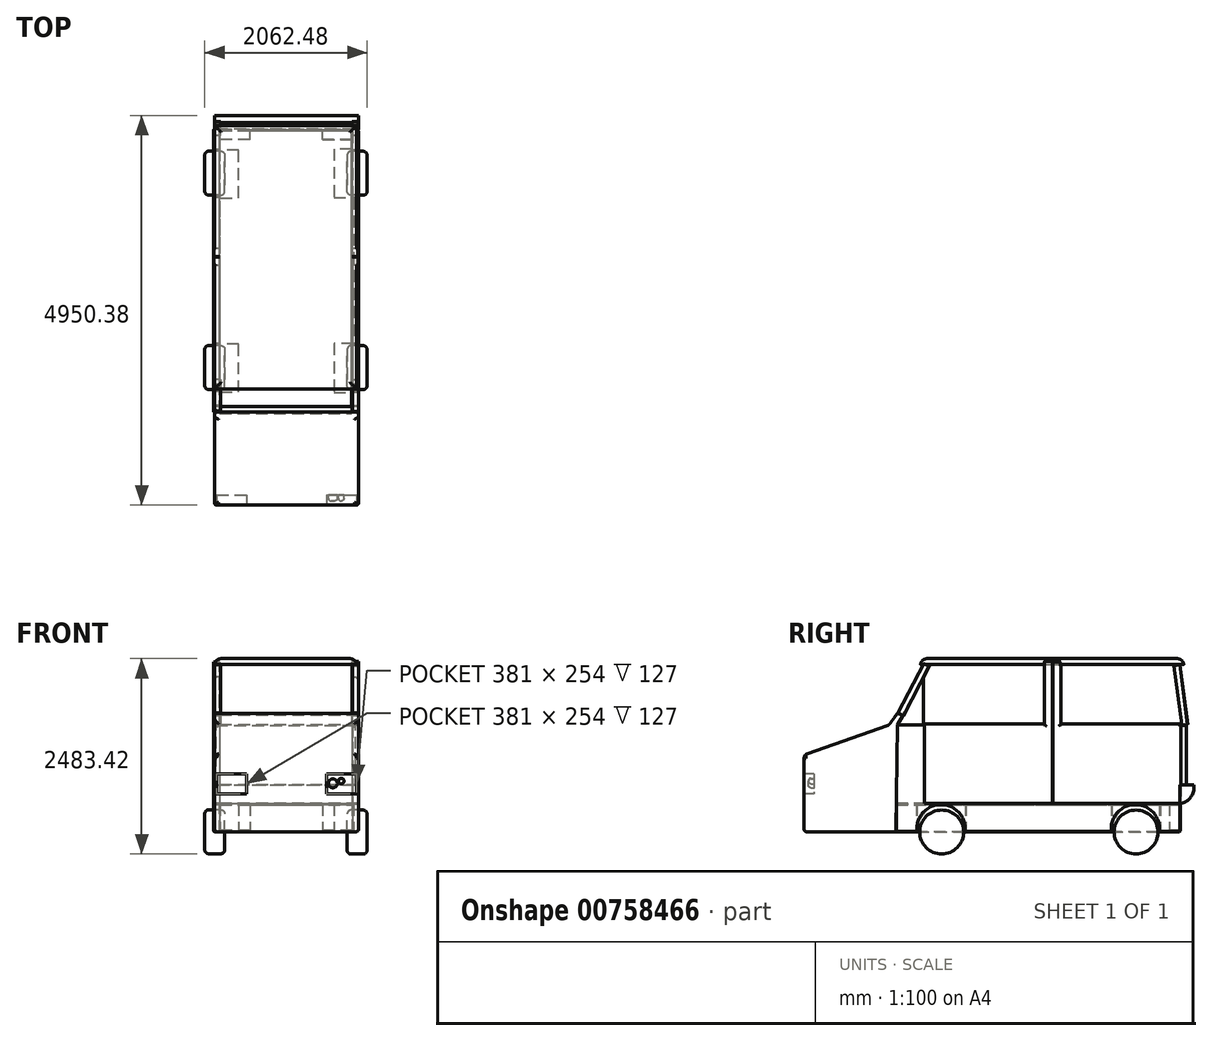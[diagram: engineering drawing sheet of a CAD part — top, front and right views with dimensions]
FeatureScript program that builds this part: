
annotation { "Feature Type Name" : "Feature", "Feature Type Description" : "" }
export const myFeature = defineFeature(function(context is Context, id is Id, definition is map)
    precondition{}
    {
        {
            var Q0;
            Q0=qCreatedBy(makeId("Top.planeOp"),FACE);
            var sketch = newSketch(context, id + "F0", { "sketchPlane" : qUnion([Q0])});
            skLineSegment(sketch, "E0.bottom", {"start": v(-913.42, 1731.15) * mm, "end": v(889.04, 1731.15) * mm});
            skLineSegment(sketch, "E0.top", {"start": v(-913.42, -1614.3) * mm, "end": v(889.04, -1614.3) * mm});
            skLineSegment(sketch, "E0.left", {"start": v(-913.42, 1731.15) * mm, "end": v(-913.42, -1614.3) * mm});
            skLineSegment(sketch, "E0.right", {"start": v(889.04, 1731.15) * mm, "end": v(889.04, -1614.3) * mm});
            skSolve(sketch);
        }
        {
            var Q0;
            Q0=makeQuery(id+"F0.imprint","IMPRINT",FACE,{"disambiguationData":[TD([[makeQuery(id+"F0.imprint","IMPRINT",EDGE,{"derivedFrom":sQuery(id+"F0.wireOp",EDGE,"E0.bottom")}),-1.0]])]});
            extrude(context, id + "F1", {"entities" : qUnion([Q0]), "surfaceOperationType" : NewSurfaceOperationType.ADD, "depth" : 76.2 * mm, "offsetDistance" : 25.4 * mm});
        }
        {
            var Q0;
            Q0=makeQuery(id+"F1.opExtrude","CAP_FACE",FACE,{"disambiguationData":[OSD([sQuery(id+"F0.wireOp",EDGE,"E0.bottom"),sQuery(id+"F0.wireOp",EDGE,"E0.top"),sQuery(id+"F0.wireOp",EDGE,"E0.left"),sQuery(id+"F0.wireOp",EDGE,"E0.right")])],"isStart":false});
            fillet(context, id + "F2", {"entities" : qUnion([Q0]), "radius" : 85.85 * mm, "tangentPropagation" : true, "allowEdgeOverflow" : false});
        }
        {
            var Q0;
            Q0=qCreatedBy(makeId("Right.planeOp"),FACE);
            var sketch = newSketch(context, id + "F3", { "sketchPlane" : qUnion([Q0])});
            skLineSegment(sketch, "E1.bottom", {"start": v(-1620.77, -101.5) * mm, "end": v(-1948.72, -732.58) * mm});
            skLineSegment(sketch, "E1.top", {"start": v(-1553.16, -136.64) * mm, "end": v(-1881.1, -767.72) * mm});
            skLineSegment(sketch, "E1.left", {"start": v(-1620.77, -101.5) * mm, "end": v(-1553.16, -136.64) * mm});
            skLineSegment(sketch, "E1.right", {"start": v(-1948.72, -732.58) * mm, "end": v(-1881.1, -767.72) * mm});
            skSolve(sketch);
        }
        {
            var Q0;
            Q0=makeQuery(id+"F3.imprint","IMPRINT",FACE,{"disambiguationData":[TD([[makeQuery(id+"F3.imprint","IMPRINT",EDGE,{"derivedFrom":sQuery(id+"F3.wireOp",EDGE,"E1.bottom")}),1.0]])]});
            extrude(context, id + "F4", {"entities" : qUnion([Q0]), "operationType" : NewBodyOperationType.ADD, "depth" : 76.2 * mm, "offsetDistance" : 25.4 * mm});
        }
        {
            var Q0;
            Q0=makeQuery(id+"F4.opExtrude","SWEPT_BODY",BODY,{"disambiguationData":[OSD([sQuery(id+"F3.wireOp",EDGE,"E1.bottom"),sQuery(id+"F3.wireOp",EDGE,"E1.top"),sQuery(id+"F3.wireOp",EDGE,"E1.left"),sQuery(id+"F3.wireOp",EDGE,"E1.right")])]});
            transform(context, id + "F5", {"entities" : qUnion([Q0]), "transformType" : TransformType.TRANSLATION_3D, "dx" : -914.4 * mm, "dy" : 0 * mm, "dz" : 116.84 * mm, "makeCopy" : false});
        }
        {
            var Q0;
            Q0=qCreatedBy(makeId("Right.planeOp"),FACE);
            var sketch = newSketch(context, id + "F6", { "sketchPlane" : qUnion([Q0])});
            skLineSegment(sketch, "E2.bottom", {"start": v(-1624.83, -94.97) * mm, "end": v(-1952.78, -726.04) * mm});
            skLineSegment(sketch, "E2.top", {"start": v(-1557.21, -130.1) * mm, "end": v(-1885.16, -761.18) * mm});
            skLineSegment(sketch, "E2.left", {"start": v(-1624.83, -94.97) * mm, "end": v(-1557.21, -130.1) * mm});
            skLineSegment(sketch, "E2.right", {"start": v(-1952.78, -726.04) * mm, "end": v(-1885.16, -761.18) * mm});
            skSolve(sketch);
        }
        {
            var Q0;
            Q0 = qSketchRegion(id + "F6", true);
            extrude(context, id + "F7", {"entities" : qUnion([Q0]), "depth" : 76.2 * mm, "offsetDistance" : 25.4 * mm});
        }
        {
            var Q0;
            Q0=makeQuery(id+"F7.opExtrude","SWEPT_BODY",BODY,{"disambiguationData":[OSD([sQuery(id+"F6.wireOp",EDGE,"E2.bottom"),sQuery(id+"F6.wireOp",EDGE,"E2.top"),sQuery(id+"F6.wireOp",EDGE,"E2.left"),sQuery(id+"F6.wireOp",EDGE,"E2.right")])]});
            transform(context, id + "F8", {"entities" : qUnion([Q0]), "transformType" : TransformType.TRANSLATION_3D, "dx" : 835.66 * mm, "dy" : -2.54 * mm, "dz" : 109.22 * mm, "makeCopy" : false});
        }
        {
            var Q0;
            Q0=qCreatedBy(makeId("Right.planeOp"),FACE);
            var sketch = newSketch(context, id + "F9", { "sketchPlane" : qUnion([Q0])});
            skLineSegment(sketch, "E3.bottom", {"start": v(1547.92, -14.01) * mm, "end": v(1647.91, -769.42) * mm});
            skLineSegment(sketch, "E3.top", {"start": v(1623.46, -4.01) * mm, "end": v(1723.46, -759.42) * mm});
            skLineSegment(sketch, "E3.left", {"start": v(1547.92, -14.01) * mm, "end": v(1623.46, -4.01) * mm});
            skLineSegment(sketch, "E3.right", {"start": v(1647.91, -769.42) * mm, "end": v(1723.46, -759.42) * mm});
            skSolve(sketch);
        }
        {
            var Q0;
            Q0 = qSketchRegion(id + "F9", true);
            extrude(context, id + "F10", {"entities" : qUnion([Q0]), "depth" : 76.2 * mm, "offsetDistance" : 25.4 * mm});
        }
        {
            var Q0;
            Q0=makeQuery(id+"F10.opExtrude","SWEPT_BODY",BODY,{"disambiguationData":[OSD([sQuery(id+"F9.wireOp",EDGE,"E3.bottom"),sQuery(id+"F9.wireOp",EDGE,"E3.top"),sQuery(id+"F9.wireOp",EDGE,"E3.left"),sQuery(id+"F9.wireOp",EDGE,"E3.right")])]});
            transform(context, id + "F11", {"entities" : qUnion([Q0]), "transformType" : TransformType.TRANSLATION_3D, "dx" : 828.04 * mm, "dy" : 0 * mm, "dz" : 0 * mm, "makeCopy" : false});
        }
        {
            var Q0;
            Q0=qCreatedBy(makeId("Right.planeOp"),FACE);
            var sketch = newSketch(context, id + "F12", { "sketchPlane" : qUnion([Q0])});
            skLineSegment(sketch, "E4.bottom", {"start": v(1549.53, -22.95) * mm, "end": v(1649.53, -778.36) * mm});
            skLineSegment(sketch, "E4.top", {"start": v(1625.08, -12.95) * mm, "end": v(1725.07, -768.36) * mm});
            skLineSegment(sketch, "E4.left", {"start": v(1549.53, -22.95) * mm, "end": v(1625.08, -12.95) * mm});
            skLineSegment(sketch, "E4.right", {"start": v(1649.53, -778.36) * mm, "end": v(1725.07, -768.36) * mm});
            skSolve(sketch);
        }
        {
            var Q0;
            Q0 = qSketchRegion(id + "F12", true);
            extrude(context, id + "F13", {"entities" : qUnion([Q0]), "depth" : 76.2 * mm, "offsetDistance" : 25.4 * mm});
        }
        {
            var Q0;
            Q0=makeQuery(id+"F13.opExtrude","SWEPT_BODY",BODY,{"disambiguationData":[OSD([sQuery(id+"F12.wireOp",EDGE,"E4.bottom"),sQuery(id+"F12.wireOp",EDGE,"E4.top"),sQuery(id+"F12.wireOp",EDGE,"E4.left"),sQuery(id+"F12.wireOp",EDGE,"E4.right")])]});
            transform(context, id + "F14", {"entities" : qUnion([Q0]), "transformType" : TransformType.TRANSLATION_3D, "dx" : -919.48 * mm, "dy" : 0 * mm, "dz" : 10.16 * mm, "makeCopy" : false});
        }
        {
            var Q0;
            Q0=qCreatedBy(makeId("Front.planeOp"),FACE);
            var sketch = newSketch(context, id + "F15", { "sketchPlane" : qUnion([Q0])});
            skLineSegment(sketch, "E5.bottom", {"start": v(910.85, -1501.62) * mm, "end": v(-917.95, -1501.62) * mm});
            skLineSegment(sketch, "E5.top", {"start": v(910.85, -1739) * mm, "end": v(-917.95, -1739) * mm});
            skLineSegment(sketch, "E5.left", {"start": v(910.85, -1501.62) * mm, "end": v(910.85, -1739) * mm});
            skLineSegment(sketch, "E5.right", {"start": v(-917.95, -1501.62) * mm, "end": v(-917.95, -1739) * mm});
            skSolve(sketch);
        }
        {
            var Q0;
            Q0 = qSketchRegion(id + "F15", true);
            extrude(context, id + "F16", {"entities" : qUnion([Q0]), "depth" : 177.8 * mm, "offsetDistance" : 25.4 * mm});
        }
        {
            var Q0;
            Q0=makeQuery(id+"F16.opExtrude","SWEPT_BODY",BODY,{"disambiguationData":[OSD([sQuery(id+"F15.wireOp",EDGE,"E5.bottom"),sQuery(id+"F15.wireOp",EDGE,"E5.top"),sQuery(id+"F15.wireOp",EDGE,"E5.left"),sQuery(id+"F15.wireOp",EDGE,"E5.right")])]});
            transform(context, id + "F17", {"entities" : qUnion([Q0]), "transformType" : TransformType.TRANSLATION_3D, "dx" : 0 * mm, "dy" : 1803.4 * mm, "dz" : -25.4 * mm, "makeCopy" : false});
        }
        {
            var Q0;
            Q0=makeQuery(id+"F16.opExtrude","CAP_EDGE",EDGE,{"disambiguationData":[OSD([sQuery(id+"F15.wireOp",EDGE,"E5.top")])],"isStart":true});
            fillet(context, id + "F18", {"entities" : qUnion([Q0]), "radius" : 202.36 * mm, "tangentPropagation" : true, "allowEdgeOverflow" : false});
        }
        {
            var Q0;
            Q0=qCreatedBy(makeId("Right.planeOp"),FACE);
            var sketch = newSketch(context, id + "F19", { "sketchPlane" : qUnion([Q0])});
            skLineSegment(sketch, "E6.bottom", {"start": v(1625.6, -744.32) * mm, "end": v(0, -744.32) * mm});
            skLineSegment(sketch, "E6.top", {"start": v(1625.6, -1751.35) * mm, "end": v(0, -1751.35) * mm});
            skLineSegment(sketch, "E6.left", {"start": v(1625.6, -744.32) * mm, "end": v(1625.6, -1751.35) * mm});
            skLineSegment(sketch, "E6.right", {"start": v(0, -744.32) * mm, "end": v(0, -1751.35) * mm});
            skLineSegment(sketch, "E7.top", {"start": v(0, 47.93) * mm, "end": v(101.6, 47.93) * mm});
            skLineSegment(sketch, "E7.left", {"start": v(0, -744.32) * mm, "end": v(0, 47.93) * mm});
            skLineSegment(sketch, "E7.right", {"start": v(101.6, -744.32) * mm, "end": v(101.6, 47.93) * mm});
            skSolve(sketch);
        }
        {
            var Q0;
            Q0 = qSketchRegion(id + "F19", true);
            extrude(context, id + "F20", {"entities" : qUnion([Q0]), "depth" : 76.2 * mm, "offsetDistance" : 25.4 * mm});
        }
        {
            var Q0;
            Q0=makeQuery(id+"F20.opExtrude","SWEPT_BODY",BODY,{"disambiguationData":[OSD([sQuery(id+"F19.wireOp",EDGE,"E6.bottom"),sQuery(id+"F19.wireOp",EDGE,"E6.top"),sQuery(id+"F19.wireOp",EDGE,"E6.left"),sQuery(id+"F19.wireOp",EDGE,"E6.right"),sQuery(id+"F19.wireOp",EDGE,"E7.top"),sQuery(id+"F19.wireOp",EDGE,"E7.left"),sQuery(id+"F19.wireOp",EDGE,"E7.right")])]});
            transform(context, id + "F21", {"entities" : qUnion([Q0]), "transformType" : TransformType.TRANSLATION_3D, "dx" : -929.64 * mm, "dy" : 10.16 * mm, "dz" : -12.7 * mm, "makeCopy" : false});
        }
        {
            var Q0;
            Q0=qCreatedBy(makeId("Right.planeOp"),FACE);
            var sketch = newSketch(context, id + "F22", { "sketchPlane" : qUnion([Q0])});
            skLineSegment(sketch, "E8.bottom", {"start": v(1625.6, -743.62) * mm, "end": v(0, -743.62) * mm});
            skLineSegment(sketch, "E8.top", {"start": v(1625.6, -1750.65) * mm, "end": v(0, -1750.65) * mm});
            skLineSegment(sketch, "E8.left", {"start": v(1625.6, -743.62) * mm, "end": v(1625.6, -1750.65) * mm});
            skLineSegment(sketch, "E8.right", {"start": v(0, -743.62) * mm, "end": v(0, -1750.65) * mm});
            skLineSegment(sketch, "E9.top", {"start": v(0, 48.63) * mm, "end": v(101.6, 48.63) * mm});
            skLineSegment(sketch, "E9.left", {"start": v(0, -743.62) * mm, "end": v(0, 48.63) * mm});
            skLineSegment(sketch, "E9.right", {"start": v(101.6, -743.62) * mm, "end": v(101.6, 48.63) * mm});
            skSolve(sketch);
        }
        {
            var Q0;
            Q0 = qSketchRegion(id + "F22", true);
            extrude(context, id + "F23", {"entities" : qUnion([Q0]), "depth" : 76.2 * mm, "offsetDistance" : 25.4 * mm});
        }
        {
            var Q0;
            Q0=makeQuery(id+"F23.opExtrude","SWEPT_BODY",BODY,{"disambiguationData":[OSD([sQuery(id+"F22.wireOp",EDGE,"E8.bottom"),sQuery(id+"F22.wireOp",EDGE,"E8.top"),sQuery(id+"F22.wireOp",EDGE,"E8.left"),sQuery(id+"F22.wireOp",EDGE,"E8.right"),sQuery(id+"F22.wireOp",EDGE,"E9.top"),sQuery(id+"F22.wireOp",EDGE,"E9.left"),sQuery(id+"F22.wireOp",EDGE,"E9.right")])]});
            transform(context, id + "F24", {"entities" : qUnion([Q0]), "transformType" : TransformType.TRANSLATION_3D, "dx" : 830.58 * mm, "dy" : 10.16 * mm, "dz" : -12.7 * mm, "makeCopy" : false});
        }
        {
            var Q0;
            Q0=qCreatedBy(makeId("Right.planeOp"),FACE);
            var sketch = newSketch(context, id + "F25", { "sketchPlane" : qUnion([Q0])});
            skLineSegment(sketch, "E10.bottom", {"start": v(9.66, -772.73) * mm, "end": v(-1615.94, -772.73) * mm});
            skLineSegment(sketch, "E10.top", {"start": v(9.66, -1779.59) * mm, "end": v(-1615.94, -1779.59) * mm});
            skLineSegment(sketch, "E10.left", {"start": v(9.66, -772.73) * mm, "end": v(9.66, -1779.59) * mm});
            skLineSegment(sketch, "E10.right", {"start": v(-1615.94, -772.73) * mm, "end": v(-1615.94, -1779.59) * mm});
            skLineSegment(sketch, "E11.top", {"start": v(-94.48, 19.52) * mm, "end": v(7.12, 19.52) * mm});
            skLineSegment(sketch, "E11.left", {"start": v(-94.48, -772.73) * mm, "end": v(-94.48, 19.52) * mm});
            skLineSegment(sketch, "E11.right", {"start": v(7.12, -772.73) * mm, "end": v(7.12, 19.52) * mm});
            skSolve(sketch);
        }
        {
            var Q0;
            Q0=makeQuery(id+"F25.imprint","IMPRINT",FACE,{"disambiguationData":[TD([[makeQuery(id+"F25.imprint","IMPRINT",EDGE,{"derivedFrom":sQuery(id+"F25.wireOp",EDGE,"E10.top")}),-1.0]])]});
            var Q1;
            Q1=makeQuery(id+"F25.imprint","IMPRINT",FACE,{"disambiguationData":[TD([[makeQuery(id+"F25.imprint","IMPRINT",EDGE,{"derivedFrom":sQuery(id+"F25.wireOp",EDGE,"E11.top")}),-1.0]])]});
            extrude(context, id + "F26", {"entities" : qUnion([Q0, Q1]), "oppositeDirection" : true, "depth" : 76.2 * mm, "offsetDistance" : 25.4 * mm});
        }
        {
            var Q0;
            Q0=makeQuery(id+"F26.opExtrude","SWEPT_BODY",BODY,{"disambiguationData":[OSD([sQuery(id+"F25.wireOp",EDGE,"E10.bottom"),sQuery(id+"F25.wireOp",EDGE,"E10.top"),sQuery(id+"F25.wireOp",EDGE,"E10.left"),sQuery(id+"F25.wireOp",EDGE,"E10.right"),sQuery(id+"F25.wireOp",EDGE,"E11.top"),sQuery(id+"F25.wireOp",EDGE,"E11.left"),sQuery(id+"F25.wireOp",EDGE,"E11.right")])]});
            transform(context, id + "F27", {"entities" : qUnion([Q0]), "transformType" : TransformType.TRANSLATION_3D, "dx" : -850.9 * mm, "dy" : 0 * mm, "dz" : 15.24 * mm, "makeCopy" : false});
        }
        {
            var Q0;
            Q0=qCreatedBy(makeId("Right.planeOp"),FACE);
            var sketch = newSketch(context, id + "F28", { "sketchPlane" : qUnion([Q0])});
            skLineSegment(sketch, "E12.bottom", {"start": v(-4.33, -770.44) * mm, "end": v(-1629.93, -770.44) * mm});
            skLineSegment(sketch, "E12.top", {"start": v(-4.33, -1777.3) * mm, "end": v(-1629.93, -1777.3) * mm});
            skLineSegment(sketch, "E12.left", {"start": v(-4.33, -770.44) * mm, "end": v(-4.33, -1777.3) * mm});
            skLineSegment(sketch, "E12.right", {"start": v(-1629.93, -770.44) * mm, "end": v(-1629.93, -1777.3) * mm});
            skLineSegment(sketch, "E13.top", {"start": v(-108.47, 21.82) * mm, "end": v(-6.87, 21.82) * mm});
            skLineSegment(sketch, "E13.left", {"start": v(-108.47, -770.44) * mm, "end": v(-108.47, 21.82) * mm});
            skLineSegment(sketch, "E13.right", {"start": v(-6.87, -770.44) * mm, "end": v(-6.87, 21.82) * mm});
            skSolve(sketch);
        }
        {
            var Q0;
            Q0 = qSketchRegion(id + "F28", true);
            extrude(context, id + "F29", {"entities" : qUnion([Q0]), "depth" : 76.2 * mm, "offsetDistance" : 25.4 * mm});
        }
        {
            var Q0;
            Q0=makeQuery(id+"F29.opExtrude","SWEPT_BODY",BODY,{"disambiguationData":[OSD([sQuery(id+"F28.wireOp",EDGE,"E12.bottom"),sQuery(id+"F28.wireOp",EDGE,"E12.top"),sQuery(id+"F28.wireOp",EDGE,"E12.left"),sQuery(id+"F28.wireOp",EDGE,"E12.right"),sQuery(id+"F28.wireOp",EDGE,"E13.top"),sQuery(id+"F28.wireOp",EDGE,"E13.left"),sQuery(id+"F28.wireOp",EDGE,"E13.right")])]});
            transform(context, id + "F30", {"entities" : qUnion([Q0]), "transformType" : TransformType.TRANSLATION_3D, "dx" : 838.2 * mm, "dy" : 12.7 * mm, "dz" : 15.24 * mm, "makeCopy" : false});
        }
        {
            var Q0;
            Q0=qCreatedBy(makeId("Right.planeOp"),FACE);
            var sketch = newSketch(context, id + "F31", { "sketchPlane" : qUnion([Q0])});
            skLineSegment(sketch, "E14", {"start": v(-1629.73, -766.93) * mm, "end": v(-1967.97, -766.93) * mm});
            skLineSegment(sketch, "E15", {"start": v(-1629.73, -766.93) * mm, "end": v(-1629.73, -162.86) * mm});
            skLineSegment(sketch, "E16", {"start": v(-1629.73, -162.86) * mm, "end": v(-1967.97, -766.93) * mm});
            skSolve(sketch);
        }
        {
            var Q0;
            Q0 = qSketchRegion(id + "F31", true);
            extrude(context, id + "F32", {"entities" : qUnion([Q0]), "depth" : 76.2 * mm, "offsetDistance" : 25.4 * mm});
        }
        {
            var Q0;
            Q0=makeQuery(id+"F32.opExtrude","SWEPT_BODY",BODY,{"disambiguationData":[OSD([sQuery(id+"F31.wireOp",EDGE,"E14"),sQuery(id+"F31.wireOp",EDGE,"E15"),sQuery(id+"F31.wireOp",EDGE,"E16")])]});
            transform(context, id + "F33", {"entities" : qUnion([Q0]), "transformType" : TransformType.TRANSLATION_3D, "dx" : 828.04 * mm, "dy" : 0 * mm, "dz" : 0 * mm, "makeCopy" : false});
        }
        {
            var Q0;
            Q0=qCreatedBy(makeId("Right.planeOp"),FACE);
            var sketch = newSketch(context, id + "F34", { "sketchPlane" : qUnion([Q0])});
            skLineSegment(sketch, "E17", {"start": v(-1630.86, -760.73) * mm, "end": v(-1969.1, -760.73) * mm});
            skLineSegment(sketch, "E18", {"start": v(-1630.86, -760.73) * mm, "end": v(-1630.86, -156.66) * mm});
            skLineSegment(sketch, "E19", {"start": v(-1630.86, -156.66) * mm, "end": v(-1969.1, -760.73) * mm});
            skSolve(sketch);
        }
        {
            var Q0;
            Q0 = qSketchRegion(id + "F34", true);
            extrude(context, id + "F35", {"entities" : qUnion([Q0]), "depth" : 76.2 * mm, "offsetDistance" : 25.4 * mm});
        }
        {
            var Q0;
            Q0=makeQuery(id+"F35.opExtrude","SWEPT_BODY",BODY,{"disambiguationData":[OSD([sQuery(id+"F34.wireOp",EDGE,"E17"),sQuery(id+"F34.wireOp",EDGE,"E18"),sQuery(id+"F34.wireOp",EDGE,"E19")])]});
            transform(context, id + "F36", {"entities" : qUnion([Q0]), "transformType" : TransformType.TRANSLATION_3D, "dx" : -914.4 * mm, "dy" : 0 * mm, "dz" : 0 * mm, "makeCopy" : false});
        }
        {
            var Q0;
            Q0=qCreatedBy(makeId("Right.planeOp"),FACE);
            var sketch = newSketch(context, id + "F37", { "sketchPlane" : qUnion([Q0])});
            skLineSegment(sketch, "E20", {"start": v(1624.35, -1763.38) * mm, "end": v(1624.35, -2119.01) * mm});
            skLineSegment(sketch, "E21", {"start": v(1624.35, -2119.01) * mm, "end": v(1361.69, -2119.01) * mm});
            skArc(sketch, "E22", {"start": v(1361.69, -2119.01) * mm, "mid": v(1059.19, -1776.84) * mm, "end": v(756.69, -2119.01) * mm});
            skLineSegment(sketch, "E23", {"start": v(-1975.22, -764.67) * mm, "end": v(-1975.22, -2119.01) * mm});
            skLineSegment(sketch, "E24", {"start": v(-1975.22, -2119.01) * mm, "end": v(-1711.82, -2119.01) * mm});
            skArc(sketch, "E25", {"start": v(-1106.82, -2119.01) * mm, "mid": v(-1409.32, -1776.84) * mm, "end": v(-1711.82, -2119.01) * mm});
            skLineSegment(sketch, "E26", {"start": v(-1106.82, -2119.01) * mm, "end": v(756.69, -2119.01) * mm});
            skLineSegment(sketch, "E27", {"start": v(-1975.22, -764.67) * mm, "end": v(-1620.55, -764.67) * mm});
            skLineSegment(sketch, "E28", {"start": v(-1620.55, -764.67) * mm, "end": v(-1620.55, -1765.04) * mm});
            skLineSegment(sketch, "E29", {"start": v(-1620.55, -1765.04) * mm, "end": v(1624.35, -1763.38) * mm});
            skSolve(sketch);
        }
        {
            var Q0;
            Q0 = qSketchRegion(id + "F37", true);
            extrude(context, id + "F38", {"entities" : qUnion([Q0]), "depth" : 76.2 * mm, "offsetDistance" : 25.4 * mm});
        }
        {
            var Q0;
            Q0=makeQuery(id+"F38.opExtrude","SWEPT_BODY",BODY,{"disambiguationData":[OSD([sQuery(id+"F37.wireOp",EDGE,"E20"),sQuery(id+"F37.wireOp",EDGE,"E21"),sQuery(id+"F37.wireOp",EDGE,"E22"),sQuery(id+"F37.wireOp",EDGE,"E23"),sQuery(id+"F37.wireOp",EDGE,"E24"),sQuery(id+"F37.wireOp",EDGE,"E25"),sQuery(id+"F37.wireOp",EDGE,"E26"),sQuery(id+"F37.wireOp",EDGE,"E27"),sQuery(id+"F37.wireOp",EDGE,"E28"),sQuery(id+"F37.wireOp",EDGE,"E29")])]});
            transform(context, id + "F39", {"entities" : qUnion([Q0]), "transformType" : TransformType.TRANSLATION_3D, "dx" : 833.12 * mm, "dy" : 0 * mm, "dz" : 0 * mm, "makeCopy" : false});
        }
        {
            var Q0;
            Q0=qCreatedBy(makeId("Right.planeOp"),FACE);
            var sketch = newSketch(context, id + "F40", { "sketchPlane" : qUnion([Q0])});
            skLineSegment(sketch, "E30", {"start": v(1632.28, -1771.88) * mm, "end": v(1632.28, -2127.5) * mm});
            skLineSegment(sketch, "E31", {"start": v(1632.28, -2127.5) * mm, "end": v(1369.62, -2127.5) * mm});
            skArc(sketch, "E32", {"start": v(1369.62, -2127.5) * mm, "mid": v(1067.12, -1785.34) * mm, "end": v(764.61, -2127.5) * mm});
            skLineSegment(sketch, "E33", {"start": v(-1967.3, -773.17) * mm, "end": v(-1967.3, -2127.5) * mm});
            skLineSegment(sketch, "E34", {"start": v(-1967.3, -2127.5) * mm, "end": v(-1703.9, -2127.5) * mm});
            skArc(sketch, "E35", {"start": v(-1098.9, -2127.5) * mm, "mid": v(-1401.4, -1785.34) * mm, "end": v(-1703.9, -2127.5) * mm});
            skLineSegment(sketch, "E36", {"start": v(-1098.9, -2127.5) * mm, "end": v(764.61, -2127.5) * mm});
            skLineSegment(sketch, "E37", {"start": v(-1967.3, -773.17) * mm, "end": v(-1612.62, -773.17) * mm});
            skLineSegment(sketch, "E38", {"start": v(-1612.62, -773.17) * mm, "end": v(-1612.62, -1773.54) * mm});
            skLineSegment(sketch, "E39", {"start": v(-1612.62, -1773.54) * mm, "end": v(1632.28, -1771.88) * mm});
            skSolve(sketch);
        }
        {
            var Q0;
            Q0 = qSketchRegion(id + "F40", true);
            extrude(context, id + "F41", {"entities" : qUnion([Q0]), "depth" : 76.2 * mm, "offsetDistance" : 25.4 * mm});
        }
        {
            var Q0;
            Q0=makeQuery(id+"F41.opExtrude","SWEPT_BODY",BODY,{"disambiguationData":[OSD([sQuery(id+"F40.wireOp",EDGE,"E30"),sQuery(id+"F40.wireOp",EDGE,"E31"),sQuery(id+"F40.wireOp",EDGE,"E32"),sQuery(id+"F40.wireOp",EDGE,"E33"),sQuery(id+"F40.wireOp",EDGE,"E34"),sQuery(id+"F40.wireOp",EDGE,"E35"),sQuery(id+"F40.wireOp",EDGE,"E36"),sQuery(id+"F40.wireOp",EDGE,"E37"),sQuery(id+"F40.wireOp",EDGE,"E38"),sQuery(id+"F40.wireOp",EDGE,"E39")])]});
            transform(context, id + "F42", {"entities" : qUnion([Q0]), "transformType" : TransformType.TRANSLATION_3D, "dx" : -929.64 * mm, "dy" : 0 * mm, "dz" : 0 * mm, "makeCopy" : false});
        }
        {
            var Q0;
            Q0=qCreatedBy(makeId("Top.planeOp"),FACE);
            var sketch = newSketch(context, id + "F43", { "sketchPlane" : qUnion([Q0])});
            skLineSegment(sketch, "E40", {"start": v(828.42, -1713.23) * mm, "end": v(828.42, -1973.46) * mm});
            skLineSegment(sketch, "E41", {"start": v(828.42, -1973.46) * mm, "end": v(-844.52, -1973.46) * mm});
            skLineSegment(sketch, "E42", {"start": v(-844.52, 1620.26) * mm, "end": v(828.42, 1620.26) * mm});
            skLineSegment(sketch, "E43", {"start": v(828.42, 1620.26) * mm, "end": v(828.42, 1378.6) * mm});
            skLineSegment(sketch, "E44", {"start": v(828.42, 1378.6) * mm, "end": v(599.16, 1378.6) * mm});
            skLineSegment(sketch, "E45", {"start": v(599.16, 1378.6) * mm, "end": v(599.16, 759) * mm});
            skLineSegment(sketch, "E46", {"start": v(599.16, 759) * mm, "end": v(847, 759) * mm});
            skLineSegment(sketch, "E47", {"start": v(847, 759) * mm, "end": v(847, -1093.62) * mm});
            skLineSegment(sketch, "E48", {"start": v(847, -1093.62) * mm, "end": v(599.16, -1093.62) * mm});
            skLineSegment(sketch, "E49", {"start": v(599.16, -1093.62) * mm, "end": v(599.16, -1719.42) * mm});
            skLineSegment(sketch, "E50", {"start": v(599.16, -1719.42) * mm, "end": v(828.42, -1713.23) * mm});
            skLineSegment(sketch, "E51", {"start": v(-844.52, -1973.46) * mm, "end": v(-844.52, -1713.23) * mm});
            skLineSegment(sketch, "E52", {"start": v(-844.52, -1713.23) * mm, "end": v(-609.07, -1713.23) * mm});
            skLineSegment(sketch, "E53", {"start": v(-609.07, -1713.23) * mm, "end": v(-609.07, -1099.82) * mm});
            skLineSegment(sketch, "E54", {"start": v(-609.07, -1099.82) * mm, "end": v(-844.52, -1099.82) * mm});
            skLineSegment(sketch, "E55", {"start": v(-844.52, -1099.82) * mm, "end": v(-844.52, 752.8) * mm});
            skLineSegment(sketch, "E56", {"start": v(-844.52, 752.8) * mm, "end": v(-609.07, 752.8) * mm});
            skLineSegment(sketch, "E57", {"start": v(-609.07, 752.8) * mm, "end": v(-609.07, 1366.22) * mm});
            skLineSegment(sketch, "E58", {"start": v(-609.07, 1366.22) * mm, "end": v(-844.52, 1366.22) * mm});
            skLineSegment(sketch, "E59", {"start": v(-844.52, 1366.22) * mm, "end": v(-844.52, 1620.26) * mm});
            skSolve(sketch);
        }
        {
            var Q0;
            Q0 = qSketchRegion(id + "F43", true);
            extrude(context, id + "F44", {"entities" : qUnion([Q0]), "depth" : 355.6 * mm, "offsetDistance" : 25.4 * mm});
        }
        {
            var Q0;
            Q0=makeQuery(id+"F44.opExtrude","SWEPT_BODY",BODY,{"disambiguationData":[OSD([sQuery(id+"F43.wireOp",EDGE,"E40"),sQuery(id+"F43.wireOp",EDGE,"E41"),sQuery(id+"F43.wireOp",EDGE,"E42"),sQuery(id+"F43.wireOp",EDGE,"E43"),sQuery(id+"F43.wireOp",EDGE,"E44"),sQuery(id+"F43.wireOp",EDGE,"E45"),sQuery(id+"F43.wireOp",EDGE,"E46"),sQuery(id+"F43.wireOp",EDGE,"E47"),sQuery(id+"F43.wireOp",EDGE,"E48"),sQuery(id+"F43.wireOp",EDGE,"E49"),sQuery(id+"F43.wireOp",EDGE,"E50"),sQuery(id+"F43.wireOp",EDGE,"E51"),sQuery(id+"F43.wireOp",EDGE,"E52"),sQuery(id+"F43.wireOp",EDGE,"E53"),sQuery(id+"F43.wireOp",EDGE,"E54"),sQuery(id+"F43.wireOp",EDGE,"E55"),sQuery(id+"F43.wireOp",EDGE,"E56"),sQuery(id+"F43.wireOp",EDGE,"E57"),sQuery(id+"F43.wireOp",EDGE,"E58"),sQuery(id+"F43.wireOp",EDGE,"E59")])]});
            transform(context, id + "F45", {"entities" : qUnion([Q0]), "transformType" : TransformType.TRANSLATION_3D, "dx" : 0 * mm, "dy" : 0 * mm, "dz" : -2125.98 * mm, "makeCopy" : false});
        }
        {
            var Q0;
            Q0=qCreatedBy(makeId("Top.planeOp"),FACE);
            var sketch = newSketch(context, id + "F46", { "sketchPlane" : qUnion([Q0])});
            skLineSegment(sketch, "E60.bottom", {"start": v(-851.82, -1980.55) * mm, "end": v(825.7, -1980.55) * mm});
            skLineSegment(sketch, "E60.top", {"start": v(-851.82, 1612.18) * mm, "end": v(825.7, 1612.18) * mm});
            skLineSegment(sketch, "E60.left", {"start": v(-851.82, -1980.55) * mm, "end": v(-851.82, 1612.18) * mm});
            skLineSegment(sketch, "E60.right", {"start": v(825.7, -1980.55) * mm, "end": v(825.7, 1612.18) * mm});
            skSolve(sketch);
        }
        {
            var Q0;
            Q0 = qSketchRegion(id + "F46", true);
            extrude(context, id + "F47", {"entities" : qUnion([Q0]), "depth" : 25.4 * mm, "offsetDistance" : 25.4 * mm});
        }
        {
            var Q0;
            Q0=makeQuery(id+"F47.opExtrude","SWEPT_BODY",BODY,{"disambiguationData":[OSD([sQuery(id+"F46.wireOp",EDGE,"E60.bottom"),sQuery(id+"F46.wireOp",EDGE,"E60.top"),sQuery(id+"F46.wireOp",EDGE,"E60.left"),sQuery(id+"F46.wireOp",EDGE,"E60.right")])]});
            transform(context, id + "F48", {"entities" : qUnion([Q0]), "transformType" : TransformType.TRANSLATION_3D, "dx" : 0 * mm, "dy" : 0 * mm, "dz" : -1780.54 * mm, "makeCopy" : false});
        }
        {
            var Q0;
            Q0=qCreatedBy(makeId("Right.planeOp"),FACE);
            var sketch = newSketch(context, id + "F49", { "sketchPlane" : qUnion([Q0])});
            skLineSegment(sketch, "E61", {"start": v(-1962, -617.43) * mm, "end": v(-2068.8, -765.92) * mm});
            skLineSegment(sketch, "E62", {"start": v(-2068.8, -765.92) * mm, "end": v(-3146.98, -1146.38) * mm});
            skLineSegment(sketch, "E63", {"start": v(-3146.98, -1146.38) * mm, "end": v(-3146.98, -2122.05) * mm});
            skLineSegment(sketch, "E64", {"start": v(-3146.98, -2122.05) * mm, "end": v(-1978.53, -2122.05) * mm});
            skLineSegment(sketch, "E65", {"start": v(-1978.53, -2122.05) * mm, "end": v(-1962, -765.92) * mm});
            skLineSegment(sketch, "E66", {"start": v(-1962, -765.92) * mm, "end": v(-1895.44, -643.06) * mm});
            skLineSegment(sketch, "E67", {"start": v(-1895.44, -643.06) * mm, "end": v(-1962, -617.43) * mm});
            skSolve(sketch);
        }
        {
            var Q0;
            Q0 = qSketchRegion(id + "F49", true);
            extrude(context, id + "F50", {"entities" : qUnion([Q0]), "depth" : 1828.8 * mm, "offsetDistance" : 25.4 * mm});
        }
        {
            var Q0;
            Q0=makeQuery(id+"F50.opExtrude","SWEPT_BODY",BODY,{"disambiguationData":[OSD([sQuery(id+"F49.wireOp",EDGE,"E61"),sQuery(id+"F49.wireOp",EDGE,"E62"),sQuery(id+"F49.wireOp",EDGE,"E63"),sQuery(id+"F49.wireOp",EDGE,"E64"),sQuery(id+"F49.wireOp",EDGE,"E65"),sQuery(id+"F49.wireOp",EDGE,"E66"),sQuery(id+"F49.wireOp",EDGE,"E67")])]});
            transform(context, id + "F51", {"entities" : qUnion([Q0]), "transformType" : TransformType.TRANSLATION_3D, "dx" : -916.94 * mm, "dy" : 0 * mm, "dz" : 0 * mm, "makeCopy" : false});
        }
        {
            var Q0;
            Q0=qCreatedBy(makeId("Right.planeOp"),FACE);
            var sketch = newSketch(context, id + "F52", { "sketchPlane" : qUnion([Q0])});
            skCircle(sketch, "E68", {"center": v(1070, -2123.2) * mm, "radius": 279.4 * mm});
            skCircle(sketch, "E69", {"center": v(-1399.13, -2123.2) * mm, "radius": 279.4 * mm});
            skSolve(sketch);
        }
        {
            var Q0;
            Q0 = qSketchRegion(id + "F52", true);
            extrude(context, id + "F53", {"entities" : qUnion([Q0]), "depth" : 254 * mm, "offsetDistance" : 25.4 * mm});
        }
        {
            var Q0;
            Q0=makeQuery(id+"F53.opExtrude","SWEPT_BODY",BODY,{"disambiguationData":[OSD([sQuery(id+"F52.wireOp",EDGE,"E68")])]});
            var Q1;
            Q1=makeQuery(id+"F53.opExtrude","SWEPT_BODY",BODY,{"disambiguationData":[OSD([sQuery(id+"F52.wireOp",EDGE,"E69")])]});
            transform(context, id + "F54", {"entities" : qUnion([Q0, Q1]), "transformType" : TransformType.TRANSLATION_3D, "dx" : -1041.4 * mm, "dy" : 0 * mm, "dz" : 0 * mm, "makeCopy" : false});
        }
        {
            var Q0;
            Q0=qCreatedBy(makeId("Right.planeOp"),FACE);
            var sketch = newSketch(context, id + "F55", { "sketchPlane" : qUnion([Q0])});
            skCircle(sketch, "E70", {"center": v(1068.66, -2127.82) * mm, "radius": 279.4 * mm});
            skCircle(sketch, "E71", {"center": v(-1400.48, -2127.82) * mm, "radius": 279.4 * mm});
            skSolve(sketch);
        }
        {
            var Q0;
            Q0 = qSketchRegion(id + "F55", true);
            extrude(context, id + "F56", {"entities" : qUnion([Q0]), "depth" : 254 * mm, "offsetDistance" : 25.4 * mm});
        }
        {
            var Q0;
            Q0=makeQuery(id+"F56.opExtrude","SWEPT_BODY",BODY,{"disambiguationData":[OSD([sQuery(id+"F55.wireOp",EDGE,"E71")])]});
            var Q1;
            Q1=makeQuery(id+"F56.opExtrude","SWEPT_BODY",BODY,{"disambiguationData":[OSD([sQuery(id+"F55.wireOp",EDGE,"E70")])]});
            transform(context, id + "F57", {"entities" : qUnion([Q0, Q1]), "transformType" : TransformType.TRANSLATION_3D, "dx" : 767.08 * mm, "dy" : 0 * mm, "dz" : 0 * mm, "makeCopy" : false});
        }
        {
            var Q0;
            Q0=makeQuery(id+"F53.opExtrude","CAP_EDGE",EDGE,{"disambiguationData":[OSD([sQuery(id+"F52.wireOp",EDGE,"E68")])],"isStart":true});
            var Q1;
            Q1=makeQuery(id+"F53.opExtrude","CAP_EDGE",EDGE,{"disambiguationData":[OSD([sQuery(id+"F52.wireOp",EDGE,"E69")])],"isStart":true});
            var Q2;
            Q2=makeQuery(id+"F53.opExtrude","CAP_EDGE",EDGE,{"disambiguationData":[OSD([sQuery(id+"F52.wireOp",EDGE,"E68")])],"isStart":false});
            var Q3;
            Q3=makeQuery(id+"F53.opExtrude","CAP_EDGE",EDGE,{"disambiguationData":[OSD([sQuery(id+"F52.wireOp",EDGE,"E69")])],"isStart":false});
            var Q4;
            Q4=makeQuery(id+"F56.opExtrude","CAP_EDGE",EDGE,{"disambiguationData":[OSD([sQuery(id+"F55.wireOp",EDGE,"E71")])],"isStart":false});
            var Q5;
            Q5=makeQuery(id+"F56.opExtrude","CAP_EDGE",EDGE,{"disambiguationData":[OSD([sQuery(id+"F55.wireOp",EDGE,"E71")])],"isStart":true});
            var Q6;
            Q6=makeQuery(id+"F56.opExtrude","CAP_EDGE",EDGE,{"disambiguationData":[OSD([sQuery(id+"F55.wireOp",EDGE,"E70")])],"isStart":true});
            var Q7;
            Q7=makeQuery(id+"F56.opExtrude","CAP_EDGE",EDGE,{"disambiguationData":[OSD([sQuery(id+"F55.wireOp",EDGE,"E70")])],"isStart":false});
            fillet(context, id + "F58", {"entities" : qUnion([Q0, Q1, Q2, Q3, Q4, Q5, Q6, Q7]), "radius" : 50.8 * mm, "tangentPropagation" : true, "allowEdgeOverflow" : false});
        }
        {
            var Q0;
            Q0=makeQuery(id+"F50.opExtrude","SWEPT_FACE",FACE,{"disambiguationData":[OSD([sQuery(id+"F49.wireOp",EDGE,"E62")])]});
            fillet(context, id + "F59", {"entities" : qUnion([Q0]), "radius" : 52.85 * mm, "tangentPropagation" : true, "allowEdgeOverflow" : false});
        }
        {
            var Q0;
            Q0=makeQuery(id+"F20.opExtrude","CAP_EDGE",EDGE,{"disambiguationData":[OSD([sQuery(id+"F19.wireOp",EDGE,"E7.right")])],"isStart":true});
            var Q1;
            Q1=makeQuery(id+"F26.opExtrude","CAP_EDGE",EDGE,{"disambiguationData":[OSD([sQuery(id+"F25.wireOp",EDGE,"E11.left")])],"isStart":false});
            var Q2;
            Q2=makeQuery(id+"F4.opExtrude","CAP_EDGE",EDGE,{"disambiguationData":[OSD([sQuery(id+"F3.wireOp",EDGE,"E1.bottom")])],"isStart":true});
            var Q3;
            Q3=makeQuery(id+"FQKj63RTNBeR8LY_5.opExtrude","CAP_EDGE",EDGE,{"disambiguationData":[OSD([sQuery(id+"FkFigYE9TCUX6iK_5.wireOp",EDGE,"t939sSEi-L39Z-RFKS-dIBj-4GTwzTyPwgOd.right")])],"isStart":true});
            var Q4;
            Q4=makeQuery(id+"F13.opExtrude","CAP_EDGE",EDGE,{"disambiguationData":[OSD([sQuery(id+"F12.wireOp",EDGE,"E4.top")])],"isStart":true});
            var Q5;
            Q5=makeQuery(id+"F41.opExtrude","CAP_EDGE",EDGE,{"disambiguationData":[OSD([sQuery(id+"F40.wireOp",EDGE,"E30")])],"isStart":true});
            var Q6;
            Q6=makeQuery(id+"F38.opExtrude","CAP_EDGE",EDGE,{"disambiguationData":[OSD([sQuery(id+"F37.wireOp",EDGE,"E20")])],"isStart":false});
            var Q7;
            Q7=makeQuery(id+"FQKj63RTNBeR8LY_5.opExtrude","CAP_EDGE",EDGE,{"disambiguationData":[OSD([sQuery(id+"FkFigYE9TCUX6iK_5.wireOp",EDGE,"t939sSEi-L39Z-RFKS-dIBj-4GTwzTyPwgOd.left")])],"isStart":true});
            var Q8;
            Q8=makeQuery(id+"F10.opExtrude","CAP_EDGE",EDGE,{"disambiguationData":[OSD([sQuery(id+"F9.wireOp",EDGE,"E3.top")])],"isStart":false});
            var Q9;
            Q9=makeQuery(id+"F23.opExtrude","CAP_EDGE",EDGE,{"disambiguationData":[OSD([sQuery(id+"F22.wireOp",EDGE,"E9.right")])],"isStart":false});
            var Q10;
            Q10=makeQuery(id+"F29.opExtrude","CAP_EDGE",EDGE,{"disambiguationData":[OSD([sQuery(id+"F28.wireOp",EDGE,"E13.left")])],"isStart":false});
            var Q11;
            Q11=makeQuery(id+"F7.opExtrude","CAP_EDGE",EDGE,{"disambiguationData":[OSD([sQuery(id+"F6.wireOp",EDGE,"E2.bottom")])],"isStart":false});
            fillet(context, id + "F60", {"entities" : qUnion([Q0, Q1, Q2, Q3, Q4, Q5, Q6, Q7, Q8, Q9, Q10, Q11]), "radius" : 25.4 * mm, "tangentPropagation" : true, "allowEdgeOverflow" : false});
        }
        {
            var Q0;
            Q0=makeQuery(id+"F50.opExtrude","CAP_EDGE",EDGE,{"disambiguationData":[OSD([sQuery(id+"F49.wireOp",EDGE,"E63")])],"isStart":true});
            var Q1;
            Q1=makeQuery(id+"F50.opExtrude","SWEPT_EDGE",EDGE,{"disambiguationData":[OSD([sQuery(id+"F49.wireOp",EDGE,"E63"),sQuery(id+"F49.wireOp",EDGE,"E64")])]});
            var Q2;
            Q2=makeQuery(id+"F50.opExtrude","CAP_EDGE",EDGE,{"disambiguationData":[OSD([sQuery(id+"F49.wireOp",EDGE,"E63")])],"isStart":false});
            var Q3;
            Q3=makeQuery(id+"F50.opExtrude","CAP_EDGE",EDGE,{"disambiguationData":[OSD([sQuery(id+"F49.wireOp",EDGE,"E64")])],"isStart":true});
            var Q4;
            Q4=makeQuery(id+"F41.opExtrude","CAP_EDGE",EDGE,{"disambiguationData":[OSD([sQuery(id+"F40.wireOp",EDGE,"E34")])],"isStart":true});
            var Q5;
            Q5=makeQuery(id+"F41.opExtrude","CAP_EDGE",EDGE,{"disambiguationData":[OSD([sQuery(id+"F40.wireOp",EDGE,"E36")])],"isStart":true});
            var Q6;
            Q6=makeQuery(id+"F41.opExtrude","CAP_EDGE",EDGE,{"disambiguationData":[OSD([sQuery(id+"F40.wireOp",EDGE,"E31")])],"isStart":true});
            var Q7;
            Q7=makeQuery(id+"F20.opExtrude","CAP_EDGE",EDGE,{"disambiguationData":[OSD([sQuery(id+"F19.wireOp",EDGE,"E6.left")])],"isStart":true});
            var Q8;
            Q8=makeQuery(id+"F23.opExtrude","CAP_EDGE",EDGE,{"disambiguationData":[OSD([sQuery(id+"F22.wireOp",EDGE,"E8.left")])],"isStart":false});
            var Q9;
            Q9=makeQuery(id+"F44.opExtrude","CAP_EDGE",EDGE,{"disambiguationData":[OSD([sQuery(id+"F43.wireOp",EDGE,"E42")])],"isStart":true});
            var Q10;
            Q10=makeQuery(id+"F38.opExtrude","CAP_EDGE",EDGE,{"disambiguationData":[OSD([sQuery(id+"F37.wireOp",EDGE,"E21")])],"isStart":false});
            var Q11;
            Q11=makeQuery(id+"F38.opExtrude","CAP_EDGE",EDGE,{"disambiguationData":[OSD([sQuery(id+"F37.wireOp",EDGE,"E26")])],"isStart":false});
            var Q12;
            Q12=makeQuery(id+"F38.opExtrude","CAP_EDGE",EDGE,{"disambiguationData":[OSD([sQuery(id+"F37.wireOp",EDGE,"E24")])],"isStart":false});
            var Q13;
            Q13=makeQuery(id+"F50.opExtrude","CAP_EDGE",EDGE,{"disambiguationData":[OSD([sQuery(id+"F49.wireOp",EDGE,"E64")])],"isStart":false});
            var Q14;
            {var subQ0=sQuery(id+"F28.wireOp",EDGE,"E12.bottom");Q14=makeQuery(id+"F29.opExtrude","CAP_EDGE",EDGE,{"disambiguationData":[OSD([subQ0]),TDD([makeQuery(id+"F28.imprint","IMPRINT",EDGE,{"disambiguationData":[TD([[makeQuery(id+"F28.imprint","INTERSECT",VERTEX,{"derivedFrom":[subQ0,sQuery(id+"F28.wireOp",EDGE,"E12.right")]}),1.0]])],"derivedFrom":subQ0})])],"isStart":false});}
            var Q15;
            Q15=makeQuery(id+"F23.opExtrude","CAP_EDGE",EDGE,{"disambiguationData":[OSD([sQuery(id+"F22.wireOp",EDGE,"E8.bottom")])],"isStart":false});
            var Q16;
            {var subQ0=sQuery(id+"F28.wireOp",EDGE,"E12.bottom");Q16=makeQuery(id+"F29.opExtrude","CAP_EDGE",EDGE,{"disambiguationData":[OSD([subQ0]),TDD([makeQuery(id+"F28.imprint","IMPRINT",EDGE,{"disambiguationData":[TD([[makeQuery(id+"F28.imprint","INTERSECT",VERTEX,{"derivedFrom":[subQ0,sQuery(id+"F28.wireOp",EDGE,"E12.right")]}),1.0]])],"derivedFrom":subQ0})])],"isStart":true});}
            var Q17;
            Q17=makeQuery(id+"F23.opExtrude","CAP_EDGE",EDGE,{"disambiguationData":[OSD([sQuery(id+"F22.wireOp",EDGE,"E8.bottom")])],"isStart":true});
            var Q18;
            {var subQ0=sQuery(id+"F25.wireOp",EDGE,"E10.bottom");Q18=makeQuery(id+"F26.opExtrude","CAP_EDGE",EDGE,{"disambiguationData":[OSD([subQ0]),TDD([makeQuery(id+"F25.imprint","IMPRINT",EDGE,{"disambiguationData":[TD([[makeQuery(id+"F25.imprint","INTERSECT",VERTEX,{"derivedFrom":[subQ0,sQuery(id+"F25.wireOp",EDGE,"E10.right")]}),1.0]])],"derivedFrom":subQ0})])],"isStart":false});}
            var Q19;
            {var subQ0=sQuery(id+"F25.wireOp",EDGE,"E10.bottom");Q19=makeQuery(id+"F26.opExtrude","CAP_EDGE",EDGE,{"disambiguationData":[OSD([subQ0]),TDD([makeQuery(id+"F25.imprint","IMPRINT",EDGE,{"disambiguationData":[TD([[makeQuery(id+"F25.imprint","INTERSECT",VERTEX,{"derivedFrom":[subQ0,sQuery(id+"F25.wireOp",EDGE,"E10.right")]}),1.0]])],"derivedFrom":subQ0})])],"isStart":true});}
            var Q20;
            Q20=makeQuery(id+"F20.opExtrude","CAP_EDGE",EDGE,{"disambiguationData":[OSD([sQuery(id+"F19.wireOp",EDGE,"E6.bottom")])],"isStart":true});
            var Q21;
            Q21=makeQuery(id+"F20.opExtrude","CAP_EDGE",EDGE,{"disambiguationData":[OSD([sQuery(id+"F19.wireOp",EDGE,"E6.bottom")])],"isStart":false});
            fillet(context, id + "F61", {"entities" : qUnion([Q0, Q1, Q2, Q3, Q4, Q5, Q6, Q7, Q8, Q9, Q10, Q11, Q12, Q13, Q14, Q15, Q16, Q17, Q18, Q19, Q20, Q21]), "radius" : 25.4 * mm, "tangentPropagation" : true, "allowEdgeOverflow" : false});
        }
        {
            var Q0;
            Q0=qCreatedBy(makeId("Front.planeOp"),FACE);
            var sketch = newSketch(context, id + "F62", { "sketchPlane" : qUnion([Q0])});
            skLineSegment(sketch, "E72.bottom", {"start": v(-899.18, -1526.36) * mm, "end": v(875.8, -1526.36) * mm});
            skLineSegment(sketch, "E72.top", {"start": v(-899.18, -770.46) * mm, "end": v(875.8, -770.46) * mm});
            skLineSegment(sketch, "E72.left", {"start": v(-899.18, -1526.36) * mm, "end": v(-899.18, -770.46) * mm});
            skLineSegment(sketch, "E72.right", {"start": v(875.8, -1526.36) * mm, "end": v(875.8, -770.46) * mm});
            skSolve(sketch);
        }
        {
            var Q0;
            Q0 = qSketchRegion(id + "F62", true);
            extrude(context, id + "F63", {"entities" : qUnion([Q0]), "depth" : 76.2 * mm, "offsetDistance" : 25.4 * mm});
        }
        {
            var Q0;
            Q0=makeQuery(id+"F63.opExtrude","SWEPT_BODY",BODY,{"disambiguationData":[OSD([sQuery(id+"F62.wireOp",EDGE,"E72.bottom"),sQuery(id+"F62.wireOp",EDGE,"E72.top"),sQuery(id+"F62.wireOp",EDGE,"E72.left"),sQuery(id+"F62.wireOp",EDGE,"E72.right")])]});
            transform(context, id + "F64", {"entities" : qUnion([Q0]), "transformType" : TransformType.TRANSLATION_3D, "dx" : 0 * mm, "dy" : 1709.42 * mm, "dz" : 0 * mm, "makeCopy" : false});
        }
        {
            var Q0;
            Q0=makeQuery(id+"F63.opExtrude","CAP_EDGE",EDGE,{"disambiguationData":[OSD([sQuery(id+"F62.wireOp",EDGE,"E72.left")])],"isStart":true});
            var Q1;
            Q1=makeQuery(id+"F63.opExtrude","CAP_EDGE",EDGE,{"disambiguationData":[OSD([sQuery(id+"F62.wireOp",EDGE,"E72.right")])],"isStart":true});
            var Q2;
            Q2=makeQuery(id+"F63.opExtrude","CAP_EDGE",EDGE,{"disambiguationData":[OSD([sQuery(id+"F62.wireOp",EDGE,"E72.top")])],"isStart":true});
            fillet(context, id + "F65", {"entities" : qUnion([Q0, Q1, Q2]), "radius" : 25.4 * mm, "tangentPropagation" : true, "allowEdgeOverflow" : false});
        }
        {
            var Q0;
            Q0=makeQuery(id+"F63.opExtrude","CAP_EDGE",EDGE,{"disambiguationData":[OSD([sQuery(id+"F62.wireOp",EDGE,"E72.top")])],"isStart":false});
            var Q1;
            {var subQ0=sQuery(id+"F22.wireOp",EDGE,"E8.left");Q1=makeQuery(id+"F61.opFillet","BLEND_EDGE",EDGE,{"blendedFrom":[makeQuery(id+"F23.opExtrude","CAP_EDGE",EDGE,{"disambiguationData":[OSD([subQ0])],"isStart":false}),makeQuery(id+"F23.opExtrude","CAP_FACE",FACE,{"disambiguationData":[OSD([sQuery(id+"F22.wireOp",EDGE,"E8.bottom"),sQuery(id+"F22.wireOp",EDGE,"E8.top"),subQ0,sQuery(id+"F22.wireOp",EDGE,"E8.right"),sQuery(id+"F22.wireOp",EDGE,"E9.top"),sQuery(id+"F22.wireOp",EDGE,"E9.left"),sQuery(id+"F22.wireOp",EDGE,"E9.right")])],"isStart":false})],"blendedInto":[makeQuery(id+"F23.opExtrude","CAP_FACE",FACE,{"disambiguationData":[OSD([sQuery(id+"F22.wireOp",EDGE,"E8.bottom"),sQuery(id+"F22.wireOp",EDGE,"E8.top"),subQ0,sQuery(id+"F22.wireOp",EDGE,"E8.right"),sQuery(id+"F22.wireOp",EDGE,"E9.top"),sQuery(id+"F22.wireOp",EDGE,"E9.left"),sQuery(id+"F22.wireOp",EDGE,"E9.right")])],"isStart":false})]});}
            var Q2;
            {var subQ0=sQuery(id+"F19.wireOp",EDGE,"E6.left");Q2=makeQuery(id+"F61.opFillet","BLEND_EDGE",EDGE,{"blendedFrom":[makeQuery(id+"F20.opExtrude","CAP_EDGE",EDGE,{"disambiguationData":[OSD([subQ0])],"isStart":true}),makeQuery(id+"F20.opExtrude","CAP_FACE",FACE,{"disambiguationData":[OSD([sQuery(id+"F19.wireOp",EDGE,"E6.bottom"),sQuery(id+"F19.wireOp",EDGE,"E6.top"),subQ0,sQuery(id+"F19.wireOp",EDGE,"E6.right"),sQuery(id+"F19.wireOp",EDGE,"E7.top"),sQuery(id+"F19.wireOp",EDGE,"E7.left"),sQuery(id+"F19.wireOp",EDGE,"E7.right")])],"isStart":true})],"blendedInto":[makeQuery(id+"F20.opExtrude","CAP_FACE",FACE,{"disambiguationData":[OSD([sQuery(id+"F19.wireOp",EDGE,"E6.bottom"),sQuery(id+"F19.wireOp",EDGE,"E6.top"),subQ0,sQuery(id+"F19.wireOp",EDGE,"E6.right"),sQuery(id+"F19.wireOp",EDGE,"E7.top"),sQuery(id+"F19.wireOp",EDGE,"E7.left"),sQuery(id+"F19.wireOp",EDGE,"E7.right")])],"isStart":true})]});}
            var Q3;
            Q3=makeQuery(id+"F41.opExtrude","CAP_EDGE",EDGE,{"disambiguationData":[OSD([sQuery(id+"F40.wireOp",EDGE,"E37")])],"isStart":true});
            var Q4;
            Q4=makeQuery(id+"F35.opExtrude","CAP_EDGE",EDGE,{"disambiguationData":[OSD([sQuery(id+"F34.wireOp",EDGE,"E18")])],"isStart":true});
            var Q5;
            Q5=makeQuery(id+"F35.opExtrude","CAP_EDGE",EDGE,{"disambiguationData":[OSD([sQuery(id+"F34.wireOp",EDGE,"E18")])],"isStart":false});
            var Q6;
            Q6=makeQuery(id+"F32.opExtrude","CAP_EDGE",EDGE,{"disambiguationData":[OSD([sQuery(id+"F31.wireOp",EDGE,"E15")])],"isStart":false});
            var Q7;
            Q7=makeQuery(id+"F32.opExtrude","CAP_EDGE",EDGE,{"disambiguationData":[OSD([sQuery(id+"F31.wireOp",EDGE,"E15")])],"isStart":true});
            fillet(context, id + "F66", {"entities" : qUnion([Q0, Q1, Q2, Q3, Q4, Q5, Q6, Q7]), "radius" : 25.4 * mm, "tangentPropagation" : true, "allowEdgeOverflow" : false});
        }
        {
            var Q0;
            {var subQ0=sQuery(id+"F0.wireOp",EDGE,"E0.right");Q0=makeQuery(id+"F2.opFillet","BLEND_EDGE",EDGE,{"blendedFrom":[makeQuery(id+"F1.opExtrude","CAP_EDGE",EDGE,{"disambiguationData":[OSD([subQ0])],"isStart":false}),makeQuery(id+"F1.opExtrude","CAP_FACE",FACE,{"disambiguationData":[OSD([sQuery(id+"F0.wireOp",EDGE,"E0.bottom"),sQuery(id+"F0.wireOp",EDGE,"E0.top"),sQuery(id+"F0.wireOp",EDGE,"E0.left"),subQ0])],"isStart":true})],"blendedInto":[makeQuery(id+"F1.opExtrude","CAP_FACE",FACE,{"disambiguationData":[OSD([sQuery(id+"F0.wireOp",EDGE,"E0.bottom"),sQuery(id+"F0.wireOp",EDGE,"E0.top"),sQuery(id+"F0.wireOp",EDGE,"E0.left"),subQ0])],"isStart":true})]});}
            var Q1;
            {var subQ0=sQuery(id+"F0.wireOp",EDGE,"E0.bottom");Q1=makeQuery(id+"F2.opFillet","BLEND_EDGE",EDGE,{"blendedFrom":[makeQuery(id+"F1.opExtrude","CAP_EDGE",EDGE,{"disambiguationData":[OSD([subQ0])],"isStart":false}),makeQuery(id+"F1.opExtrude","CAP_FACE",FACE,{"disambiguationData":[OSD([subQ0,sQuery(id+"F0.wireOp",EDGE,"E0.top"),sQuery(id+"F0.wireOp",EDGE,"E0.left"),sQuery(id+"F0.wireOp",EDGE,"E0.right")])],"isStart":true})],"blendedInto":[makeQuery(id+"F1.opExtrude","CAP_FACE",FACE,{"disambiguationData":[OSD([subQ0,sQuery(id+"F0.wireOp",EDGE,"E0.top"),sQuery(id+"F0.wireOp",EDGE,"E0.left"),sQuery(id+"F0.wireOp",EDGE,"E0.right")])],"isStart":true})]});}
            var Q2;
            {var subQ0=sQuery(id+"F0.wireOp",EDGE,"E0.left");Q2=makeQuery(id+"F2.opFillet","BLEND_EDGE",EDGE,{"blendedFrom":[makeQuery(id+"F1.opExtrude","CAP_EDGE",EDGE,{"disambiguationData":[OSD([subQ0])],"isStart":false}),makeQuery(id+"F1.opExtrude","CAP_FACE",FACE,{"disambiguationData":[OSD([sQuery(id+"F0.wireOp",EDGE,"E0.bottom"),sQuery(id+"F0.wireOp",EDGE,"E0.top"),subQ0,sQuery(id+"F0.wireOp",EDGE,"E0.right")])],"isStart":true})],"blendedInto":[makeQuery(id+"F1.opExtrude","CAP_FACE",FACE,{"disambiguationData":[OSD([sQuery(id+"F0.wireOp",EDGE,"E0.bottom"),sQuery(id+"F0.wireOp",EDGE,"E0.top"),subQ0,sQuery(id+"F0.wireOp",EDGE,"E0.right")])],"isStart":true})]});}
            var Q3;
            {var subQ0=sQuery(id+"F0.wireOp",EDGE,"E0.top");Q3=makeQuery(id+"F2.opFillet","BLEND_EDGE",EDGE,{"blendedFrom":[makeQuery(id+"F1.opExtrude","CAP_EDGE",EDGE,{"disambiguationData":[OSD([subQ0])],"isStart":false}),makeQuery(id+"F1.opExtrude","CAP_FACE",FACE,{"disambiguationData":[OSD([sQuery(id+"F0.wireOp",EDGE,"E0.bottom"),subQ0,sQuery(id+"F0.wireOp",EDGE,"E0.left"),sQuery(id+"F0.wireOp",EDGE,"E0.right")])],"isStart":true})],"blendedInto":[makeQuery(id+"F1.opExtrude","CAP_FACE",FACE,{"disambiguationData":[OSD([sQuery(id+"F0.wireOp",EDGE,"E0.bottom"),subQ0,sQuery(id+"F0.wireOp",EDGE,"E0.left"),sQuery(id+"F0.wireOp",EDGE,"E0.right")])],"isStart":true})]});}
            fillet(context, id + "F67", {"entities" : qUnion([Q0, Q1, Q2, Q3]), "radius" : 3.94 * mm, "tangentPropagation" : true, "allowEdgeOverflow" : false});
        }
        {
            var Q0;
            Q0=makeQuery(id+"F50.opExtrude","SWEPT_FACE",FACE,{"disambiguationData":[OSD([sQuery(id+"F49.wireOp",EDGE,"E63")])]});
            var sketch = newSketch(context, id + "F68", { "sketchPlane" : qUnion([Q0])});
            skLineSegment(sketch, "E73.bottom", {"start": v(-890, -1388.64) * mm, "end": v(-509, -1388.64) * mm});
            skLineSegment(sketch, "E73.top", {"start": v(-890, -1642.64) * mm, "end": v(-509, -1642.64) * mm});
            skLineSegment(sketch, "E73.left", {"start": v(-890, -1388.64) * mm, "end": v(-890, -1642.64) * mm});
            skLineSegment(sketch, "E73.right", {"start": v(-509, -1388.64) * mm, "end": v(-509, -1642.64) * mm});
            skLineSegment(sketch, "E74.bottom", {"start": v(505.46, -1391.06) * mm, "end": v(886.46, -1391.06) * mm});
            skLineSegment(sketch, "E74.top", {"start": v(505.46, -1645.06) * mm, "end": v(886.46, -1645.06) * mm});
            skLineSegment(sketch, "E74.left", {"start": v(505.46, -1391.06) * mm, "end": v(505.46, -1645.06) * mm});
            skLineSegment(sketch, "E74.right", {"start": v(886.46, -1391.06) * mm, "end": v(886.46, -1645.06) * mm});
            skSolve(sketch);
        }
        {
            var Q0;
            Q0 = qSketchRegion(id + "F68", true);
            extrude(context, id + "F69", {"entities" : qUnion([Q0]), "operationType" : NewBodyOperationType.REMOVE, "oppositeDirection" : true, "depth" : 127 * mm, "offsetDistance" : 25.4 * mm});
        }
        {
            var Q0;
            Q0=makeQuery(id+"F44.opExtrude","SWEPT_FACE",FACE,{"disambiguationData":[OSD([sQuery(id+"F43.wireOp",EDGE,"E42")])]});
            var sketch = newSketch(context, id + "F70", { "sketchPlane" : qUnion([Q0])});
            skLineSegment(sketch, "E75.bottom", {"start": v(-828.42, -1770.38) * mm, "end": v(-455.76, -1770.38) * mm});
            skLineSegment(sketch, "E75.top", {"start": v(-828.42, -2100.58) * mm, "end": v(-455.76, -2100.58) * mm});
            skLineSegment(sketch, "E75.left", {"start": v(-828.42, -1770.38) * mm, "end": v(-828.42, -2100.58) * mm});
            skLineSegment(sketch, "E75.right", {"start": v(-455.76, -1770.38) * mm, "end": v(-455.76, -2100.58) * mm});
            skLineSegment(sketch, "E76.bottom", {"start": v(844.52, -1770.38) * mm, "end": v(466.54, -1770.38) * mm});
            skLineSegment(sketch, "E76.top", {"start": v(844.52, -2100.58) * mm, "end": v(466.54, -2100.58) * mm});
            skLineSegment(sketch, "E76.left", {"start": v(844.52, -1770.38) * mm, "end": v(844.52, -2100.58) * mm});
            skLineSegment(sketch, "E76.right", {"start": v(466.54, -1770.38) * mm, "end": v(466.54, -2100.58) * mm});
            skSolve(sketch);
        }
        {
            var Q0;
            Q0 = qSketchRegion(id + "F70", true);
            extrude(context, id + "F71", {"entities" : qUnion([Q0]), "operationType" : NewBodyOperationType.REMOVE, "oppositeDirection" : true, "depth" : 127 * mm, "offsetDistance" : 25.4 * mm});
        }
        {
            var Q0;
            Q0=makeQuery(id+"F1.opExtrude","SWEPT_BODY",BODY,{"disambiguationData":[OSD([sQuery(id+"F0.wireOp",EDGE,"E0.bottom"),sQuery(id+"F0.wireOp",EDGE,"E0.top"),sQuery(id+"F0.wireOp",EDGE,"E0.left"),sQuery(id+"F0.wireOp",EDGE,"E0.right")])]});
            transform(context, id + "F72", {"entities" : qUnion([Q0]), "transformType" : TransformType.TRANSLATION_3D, "dx" : -2.54 * mm, "dy" : -55.88 * mm, "dz" : 0 * mm, "makeCopy" : false});
        }
        {
            var Q0;
            Q0=makeQuery(id+"F68.imprint","IMPRINT",FACE,{"disambiguationData":[TD([[makeQuery(id+"F68.imprint","IMPRINT",EDGE,{"derivedFrom":sQuery(id+"F68.wireOp",EDGE,"E74.bottom")}),-1.0]])]});
            var sketch = newSketch(context, id + "F73", { "sketchPlane" : qUnion([Q0])});
            skCircle(sketch, "E77", {"center": v(585.8, -1509.18) * mm, "radius": 56.52 * mm});
            skCircle(sketch, "E78", {"center": v(691.57, -1479.24) * mm, "radius": 35.53 * mm});
            skSolve(sketch);
        }
        {
            var Q0;
            Q0 = qSketchRegion(id + "F73", true);
            extrude(context, id + "F74", {"entities" : qUnion([Q0]), "operationType" : NewBodyOperationType.ADD, "depth" : 76.2 * mm, "offsetDistance" : 25.4 * mm});
        }
        {
            var Q0;
            Q0=makeQuery(id+"F74.opExtrude","SWEPT_BODY",BODY,{"disambiguationData":[OSD([sQuery(id+"F73.wireOp",EDGE,"E78")])]});
            var Q1;
            Q1=makeQuery(id+"F74.opExtrude","SWEPT_BODY",BODY,{"disambiguationData":[OSD([sQuery(id+"F73.wireOp",EDGE,"E77")])]});
            transform(context, id + "F75", {"entities" : qUnion([Q0, Q1]), "transformType" : TransformType.TRANSLATION_3D, "dx" : 0 * mm, "dy" : 129.54 * mm, "dz" : 0 * mm, "makeCopy" : false});
        }
        {
            var Q0;
            Q0=makeQuery(id+"F74.opExtrude","CAP_EDGE",EDGE,{"disambiguationData":[OSD([sQuery(id+"F73.wireOp",EDGE,"E77")])],"isStart":false});
            var Q1;
            Q1=makeQuery(id+"F74.opExtrude","CAP_EDGE",EDGE,{"disambiguationData":[OSD([sQuery(id+"F73.wireOp",EDGE,"E78")])],"isStart":false});
            fillet(context, id + "F76", {"entities" : qUnion([Q0, Q1]), "radius" : 33.1 * mm, "tangentPropagation" : true, "allowEdgeOverflow" : false});
        }
    });
